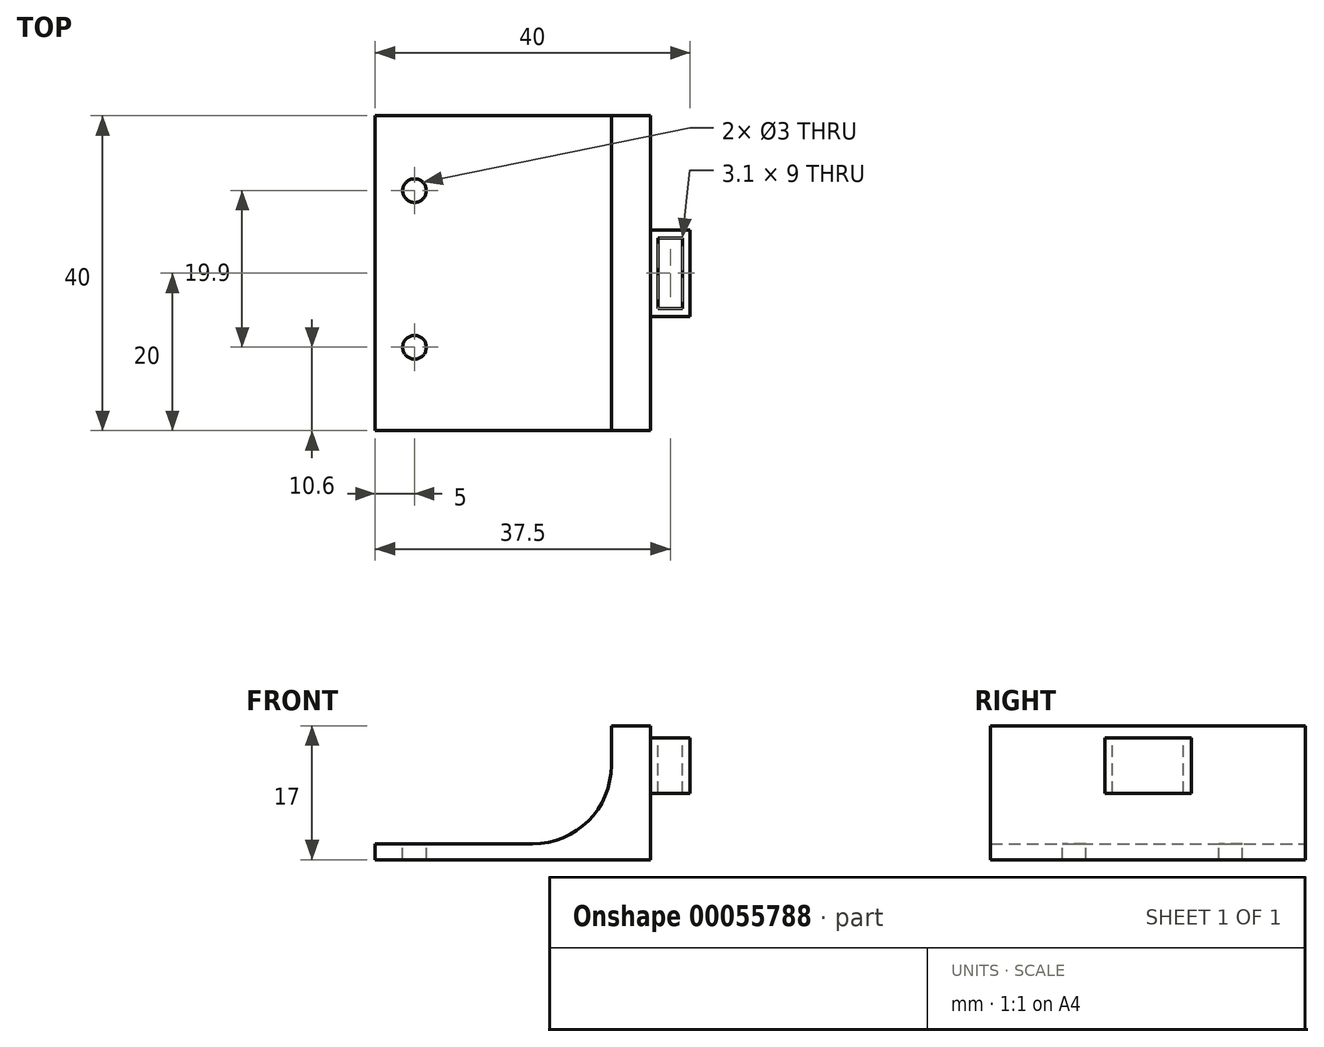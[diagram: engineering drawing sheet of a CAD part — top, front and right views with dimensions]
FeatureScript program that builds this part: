
annotation { "Feature Type Name" : "Feature", "Feature Type Description" : "" }
export const myFeature = defineFeature(function(context is Context, id is Id, definition is map)
    precondition{}
    {
        {
            var Q0;
            Q0=qCreatedBy(makeId("Front.planeOp"),FACE);
            var sketch = newSketch(context, id + "F0", { "sketchPlane" : qUnion([Q0])});
            skLineSegment(sketch, "E0.bottom", {"start": v(-5, 0) * mm, "end": v(-35, 0) * mm});
            skLineSegment(sketch, "E0.top", {"start": v(0, -2) * mm, "end": v(-35, -2) * mm});
            skLineSegment(sketch, "E0.left", {"start": v(0, 0) * mm, "end": v(0, -2) * mm});
            skLineSegment(sketch, "E0.right", {"start": v(-35, 0) * mm, "end": v(-35, -2) * mm});
            skPoint(sketch, "E1.oppositeSnap0", {"position": v(0, -1) * mm});
            skLineSegment(sketch, "E1.bottom", {"start": v(-5, -2) * mm, "end": v(0, -2) * mm});
            skLineSegment(sketch, "E1.top", {"start": v(-5, 15) * mm, "end": v(0, 15) * mm});
            skLineSegment(sketch, "E1.left", {"start": v(-5, 0) * mm, "end": v(-5, 15) * mm});
            skLineSegment(sketch, "E1.right", {"start": v(0, -2) * mm, "end": v(0, 15) * mm});
            skSolve(sketch);
        }
        {
            var Q0;
            Q0 = qSketchRegion(id + "F0", true);
            extrude(context, id + "F1", {"entities" : qUnion([Q0]), "depth" : 40 * mm});
        }
        {
            var Q0;
            Q0=makeQuery(id+"F1.opExtrude","SWEPT_EDGE",EDGE,{"disambiguationData":[OSD([sQuery(id+"F0.wireOp",EDGE,"E0.bottom"),sQuery(id+"F0.wireOp",EDGE,"E1.left")])]});
            fillet(context, id + "F2", {"entities" : qUnion([Q0]), "radius" : 10 * mm, "tangentPropagation" : true, "allowEdgeOverflow" : false});
        }
        {
            var Q0;
            Q0=makeQuery(id+"F1.opExtrude","SWEPT_FACE",FACE,{"disambiguationData":[OSD([sQuery(id+"F0.wireOp",EDGE,"E0.bottom")])]});
            var sketch = newSketch(context, id + "F3", { "sketchPlane" : qUnion([Q0])});
            skCircle(sketch, "E2", {"center": v(-30, -9.5) * mm, "radius": 1.5 * mm});
            skCircle(sketch, "E3", {"center": v(-30, -29.4) * mm, "radius": 1.5 * mm});
            skSolve(sketch);
        }
        {
            var Q0;
            Q0=makeQuery(id+"F3.imprint","IMPRINT",FACE,{"disambiguationData":[TD([[makeQuery(id+"F3.imprint","IMPRINT",EDGE,{"derivedFrom":sQuery(id+"F3.wireOp",EDGE,"E2")}),1.0]])]});
            var Q1;
            Q1=makeQuery(id+"F3.imprint","IMPRINT",FACE,{"disambiguationData":[TD([[makeQuery(id+"F3.imprint","IMPRINT",EDGE,{"derivedFrom":sQuery(id+"F3.wireOp",EDGE,"E3")}),1.0]])]});
            extrude(context, id + "F4", {"entities" : qUnion([Q0, Q1]), "operationType" : NewBodyOperationType.REMOVE, "oppositeDirection" : true, "depth" : 6 * mm});
        }
        {
            var Q0;
            Q0=makeQuery(id+"F1.opExtrude","SWEPT_FACE",FACE,{"disambiguationData":[OSD([sQuery(id+"F0.wireOp",EDGE,"E1.right")])]});
            var sketch = newSketch(context, id + "F5", { "sketchPlane" : qUnion([Q0])});
            skLineSegment(sketch, "E4.rect.bottom", {"start": v(-14.5, 6.43) * mm, "end": v(-25.5, 6.43) * mm});
            skLineSegment(sketch, "E4.rect.top", {"start": v(-14.5, 13.45) * mm, "end": v(-25.5, 13.45) * mm});
            skLineSegment(sketch, "E4.rect.left", {"start": v(-14.5, 6.43) * mm, "end": v(-14.5, 13.45) * mm});
            skLineSegment(sketch, "E4.rect.right", {"start": v(-25.5, 6.43) * mm, "end": v(-25.5, 13.45) * mm});
            skPoint(sketch, "E4.rect.middle", {"position": v(-20, 9.94) * mm});
            skPoint(sketch, "E4.rect.middle.positionSnap0", {"position": v(-20, 15) * mm});
            skPoint(sketch, "E4.rect.centerSnap0", {"position": v(-20, 15) * mm});
            skSolve(sketch);
        }
        {
            var Q0;
            Q0 = qSketchRegion(id + "F5", true);
            extrude(context, id + "F6", {"entities" : qUnion([Q0]), "operationType" : NewBodyOperationType.ADD, "depth" : 5 * mm});
        }
        {
            var Q0;
            Q0=makeQuery(id+"F6.opExtrude","SWEPT_FACE",FACE,{"disambiguationData":[OSD([sQuery(id+"F5.wireOp",EDGE,"E4.rect.top")])]});
            var sketch = newSketch(context, id + "F7", { "sketchPlane" : qUnion([Q0])});
            skLineSegment(sketch, "E5", {"start": v(2.5, -25.5) * mm, "end": v(2.5, -14.5) * mm, "construction": true});
            skLineSegment(sketch, "E6.rect.bottom", {"start": v(4.05, -15.5) * mm, "end": v(0.95, -15.5) * mm});
            skLineSegment(sketch, "E6.rect.top", {"start": v(4.05, -24.5) * mm, "end": v(0.95, -24.5) * mm});
            skLineSegment(sketch, "E6.rect.left", {"start": v(4.05, -15.5) * mm, "end": v(4.05, -24.5) * mm});
            skLineSegment(sketch, "E6.rect.right", {"start": v(0.95, -15.5) * mm, "end": v(0.95, -24.5) * mm});
            skPoint(sketch, "E6.rect.middle", {"position": v(2.5, -20) * mm});
            skSolve(sketch);
        }
        {
            var Q0;
            Q0=makeQuery(id+"F7.imprint","IMPRINT",FACE,{"disambiguationData":[TD([[makeQuery(id+"F7.imprint","IMPRINT",EDGE,{"derivedFrom":sQuery(id+"F7.wireOp",EDGE,"E6.rect.bottom")}),1.0]])]});
            extrude(context, id + "F8", {"entities" : qUnion([Q0]), "operationType" : NewBodyOperationType.REMOVE, "oppositeDirection" : true, "depth" : 25 * mm});
        }
    });
